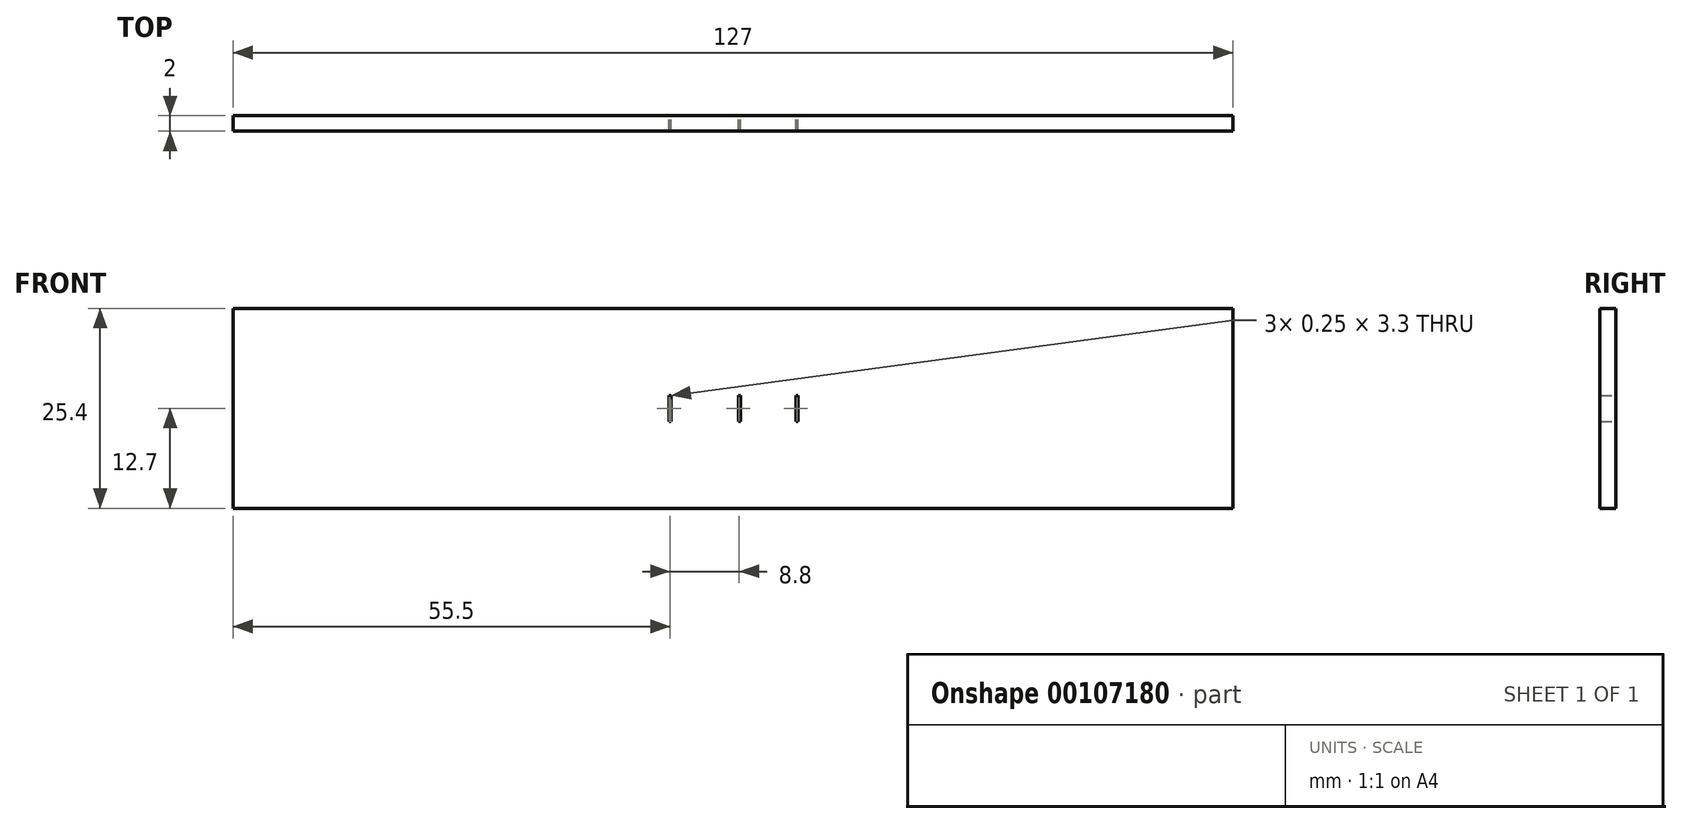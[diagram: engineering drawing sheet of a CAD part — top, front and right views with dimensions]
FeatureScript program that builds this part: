
annotation { "Feature Type Name" : "Feature", "Feature Type Description" : "" }
export const myFeature = defineFeature(function(context is Context, id is Id, definition is map)
    precondition{}
    {
        {
            var Q0;
            Q0=qCreatedBy(makeId("Front.planeOp"),FACE);
            var sketch = newSketch(context, id + "F0", { "sketchPlane" : qUnion([Q0])});
            skLineSegment(sketch, "E0.bottom", {"start": v(-63.5, 12.7) * mm, "end": v(63.5, 12.7) * mm});
            skLineSegment(sketch, "E0.top", {"start": v(-63.5, -12.7) * mm, "end": v(63.5, -12.7) * mm});
            skLineSegment(sketch, "E0.left", {"start": v(-63.5, 12.7) * mm, "end": v(-63.5, -12.7) * mm});
            skLineSegment(sketch, "E0.right", {"start": v(63.5, 12.7) * mm, "end": v(63.5, -12.7) * mm});
            skPoint(sketch, "E0.middle", {"position": v(0, 0) * mm});
            skLineSegment(sketch, "E1", {"start": v(-9.9, 0) * mm, "end": v(9.9, 0) * mm});
            skPoint(sketch, "E2", {"position": v(-8, 0) * mm});
            skPoint(sketch, "E3", {"position": v(0.8, 0) * mm});
            skPoint(sketch, "E4", {"position": v(8.1, 0) * mm});
            skLineSegment(sketch, "E5.bottom", {"start": v(7.97, 1.65) * mm, "end": v(8.23, 1.65) * mm});
            skLineSegment(sketch, "E5.top", {"start": v(7.97, -1.65) * mm, "end": v(8.23, -1.65) * mm});
            skLineSegment(sketch, "E5.left", {"start": v(7.97, 1.65) * mm, "end": v(7.97, -1.65) * mm});
            skLineSegment(sketch, "E5.right", {"start": v(8.23, 1.65) * mm, "end": v(8.23, -1.65) * mm});
            skLineSegment(sketch, "E6.bottom", {"start": v(-8.13, 1.65) * mm, "end": v(-7.87, 1.65) * mm});
            skLineSegment(sketch, "E6.top", {"start": v(-8.13, -1.65) * mm, "end": v(-7.87, -1.65) * mm});
            skLineSegment(sketch, "E6.left", {"start": v(-8.13, 1.65) * mm, "end": v(-8.13, -1.65) * mm});
            skLineSegment(sketch, "E6.right", {"start": v(-7.87, 1.65) * mm, "end": v(-7.87, -1.65) * mm});
            skLineSegment(sketch, "E7.bottom", {"start": v(0.67, 1.65) * mm, "end": v(0.93, 1.65) * mm});
            skLineSegment(sketch, "E7.top", {"start": v(0.67, -1.65) * mm, "end": v(0.93, -1.65) * mm});
            skLineSegment(sketch, "E7.left", {"start": v(0.67, 1.65) * mm, "end": v(0.67, -1.65) * mm});
            skLineSegment(sketch, "E7.right", {"start": v(0.93, 1.65) * mm, "end": v(0.93, -1.65) * mm});
            skSolve(sketch);
        }
        {
            var Q0;
            Q0=makeQuery(id+"F0.imprint","IMPRINT",FACE,{"disambiguationData":[TD([[makeQuery(id+"F0.imprint","IMPRINT",EDGE,{"derivedFrom":sQuery(id+"F0.wireOp",EDGE,"E0.bottom")}),-1.0]])]});
            extrude(context, id + "F1", {"entities" : qUnion([Q0]), "depth" : 2 * mm});
        }
    });
